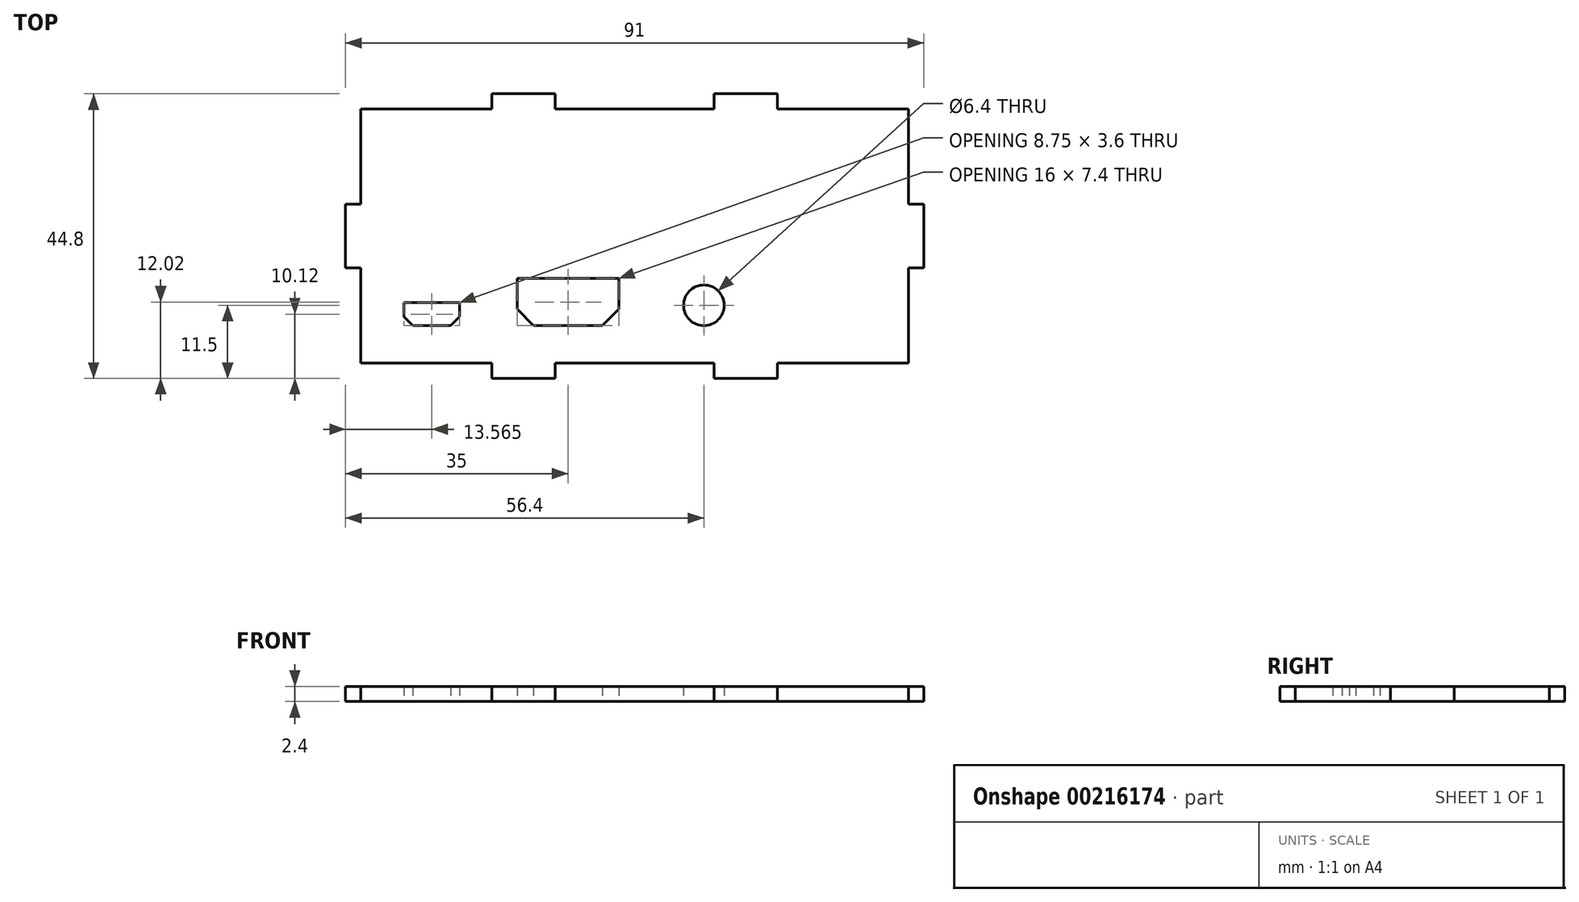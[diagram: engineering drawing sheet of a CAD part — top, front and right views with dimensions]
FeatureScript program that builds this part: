
annotation { "Feature Type Name" : "Feature", "Feature Type Description" : "" }
export const myFeature = defineFeature(function(context is Context, id is Id, definition is map)
    precondition{}
    {
        {
            var Q0;
            Q0=qCreatedBy(makeId("Top.planeOp"),FACE);
            var sketch = newSketch(context, id + "F0", { "sketchPlane" : qUnion([Q0])});
            skLineSegment(sketch, "E0.bottom", {"start": v(43.1, 20) * mm, "end": v(22.5, 20) * mm});
            skLineSegment(sketch, "E0.top", {"start": v(43.1, -20) * mm, "end": v(22.5, -20) * mm});
            skLineSegment(sketch, "E0.left", {"start": v(43.1, 20) * mm, "end": v(43.1, 5) * mm});
            skLineSegment(sketch, "E0.right", {"start": v(-43.1, 20) * mm, "end": v(-43.1, 5) * mm});
            skPoint(sketch, "E0.middle", {"position": v(0, 0) * mm});
            skLineSegment(sketch, "E1.bottom", {"start": v(-12.5, 22.4) * mm, "end": v(-22.5, 22.4) * mm});
            skLineSegment(sketch, "E1.left", {"start": v(-12.5, 22.4) * mm, "end": v(-12.5, 20) * mm});
            skLineSegment(sketch, "E1.right", {"start": v(-22.5, 22.4) * mm, "end": v(-22.5, 20) * mm});
            skPoint(sketch, "E1.middle", {"position": v(-17.5, 20) * mm});
            skLineSegment(sketch, "E2.bottom", {"start": v(22.5, 22.4) * mm, "end": v(12.5, 22.4) * mm});
            skLineSegment(sketch, "E2.left", {"start": v(22.5, 22.4) * mm, "end": v(22.5, 20) * mm});
            skLineSegment(sketch, "E2.right", {"start": v(12.5, 22.4) * mm, "end": v(12.5, 20) * mm});
            skPoint(sketch, "E2.middle", {"position": v(17.5, 20) * mm});
            skLineSegment(sketch, "E3.bottom", {"start": v(45.5, 5) * mm, "end": v(43.1, 5) * mm});
            skLineSegment(sketch, "E3.top", {"start": v(45.5, -5) * mm, "end": v(43.1, -5) * mm});
            skLineSegment(sketch, "E3.left", {"start": v(45.5, 5) * mm, "end": v(45.5, -5) * mm});
            skPoint(sketch, "E3.middle", {"position": v(43.1, 0) * mm});
            skLineSegment(sketch, "E4.top", {"start": v(22.5, -22.4) * mm, "end": v(12.5, -22.4) * mm});
            skLineSegment(sketch, "E4.left", {"start": v(22.5, -20) * mm, "end": v(22.5, -22.4) * mm});
            skLineSegment(sketch, "E4.right", {"start": v(12.5, -20) * mm, "end": v(12.5, -22.4) * mm});
            skPoint(sketch, "E4.middle", {"position": v(17.5, -20) * mm});
            skLineSegment(sketch, "E5.top", {"start": v(-12.5, -22.4) * mm, "end": v(-22.5, -22.4) * mm});
            skLineSegment(sketch, "E5.left", {"start": v(-12.5, -20) * mm, "end": v(-12.5, -22.4) * mm});
            skLineSegment(sketch, "E5.right", {"start": v(-22.5, -20) * mm, "end": v(-22.5, -22.4) * mm});
            skPoint(sketch, "E5.middle", {"position": v(-17.5, -20) * mm});
            skLineSegment(sketch, "E6.bottom", {"start": v(-45.5, 5) * mm, "end": v(-43.1, 5) * mm});
            skLineSegment(sketch, "E6.top", {"start": v(-45.5, -5) * mm, "end": v(-43.1, -5) * mm});
            skLineSegment(sketch, "E6.left", {"start": v(-45.5, 5) * mm, "end": v(-45.5, -5) * mm});
            skPoint(sketch, "E6.middle", {"position": v(-43.1, 0) * mm});
            skLineSegment(sketch, "E7.trimOffspring", {"start": v(-22.5, 20) * mm, "end": v(-43.1, 20) * mm});
            skLineSegment(sketch, "E8.trimOffspring", {"start": v(43.1, -5) * mm, "end": v(43.1, -20) * mm});
            skLineSegment(sketch, "E9.trimOffspring", {"start": v(12.5, -20) * mm, "end": v(-12.5, -20) * mm});
            skLineSegment(sketch, "E10.trimOffspring", {"start": v(-22.5, -20) * mm, "end": v(-43.1, -20) * mm});
            skLineSegment(sketch, "E11.trimOffspring", {"start": v(-43.1, -5) * mm, "end": v(-43.1, -20) * mm});
            skLineSegment(sketch, "E12", {"start": v(-12.5, 20) * mm, "end": v(12.5, 20) * mm});
            skLineSegment(sketch, "E13.bottom", {"start": v(-36.31, -10.48) * mm, "end": v(-27.56, -10.48) * mm});
            skLineSegment(sketch, "E13.top", {"start": v(-34.9, -14.08) * mm, "end": v(-28.97, -14.08) * mm});
            skLineSegment(sketch, "E13.right", {"start": v(-27.56, -10.48) * mm, "end": v(-27.56, -12.67) * mm});
            skLineSegment(sketch, "E14.bottom", {"start": v(-18.5, -6.68) * mm, "end": v(-2.5, -6.68) * mm});
            skLineSegment(sketch, "E14.top", {"start": v(-15.93, -14.08) * mm, "end": v(-5.07, -14.08) * mm});
            skLineSegment(sketch, "E14.left", {"start": v(-18.5, -6.68) * mm, "end": v(-18.5, -11.51) * mm});
            skLineSegment(sketch, "E14.right", {"start": v(-2.5, -6.68) * mm, "end": v(-2.5, -11.5) * mm});
            skCircle(sketch, "E15", {"center": v(10.9, -10.9) * mm, "radius": 3.2 * mm});
            skLineSegment(sketch, "E16", {"start": v(-27.56, -12.67) * mm, "end": v(-28.97, -14.08) * mm});
            skLineSegment(sketch, "E17", {"start": v(-18.5, -11.51) * mm, "end": v(-15.93, -14.08) * mm});
            skLineSegment(sketch, "E18", {"start": v(-2.5, -11.5) * mm, "end": v(-5.07, -14.08) * mm});
            skLineSegment(sketch, "E19", {"start": v(-36.31, -10.48) * mm, "end": v(-36.31, -12.67) * mm});
            skLineSegment(sketch, "E20", {"start": v(-34.9, -14.08) * mm, "end": v(-36.31, -12.67) * mm});
            skPoint(sketch, "E21", {"position": v(-31.94, -10.48) * mm});
            skPoint(sketch, "E22", {"position": v(-31.93, -14.08) * mm});
            skSolve(sketch);
        }
        {
            var Q0;
            Q0=makeQuery(id+"F0.imprint","IMPRINT",FACE,{"disambiguationData":[TD([[makeQuery(id+"F0.imprint","IMPRINT",EDGE,{"derivedFrom":sQuery(id+"F0.wireOp",EDGE,"E0.bottom")}),1.0]])]});
            extrude(context, id + "F1", {"entities" : qUnion([Q0]), "depth" : 2.4 * mm});
        }
    });
